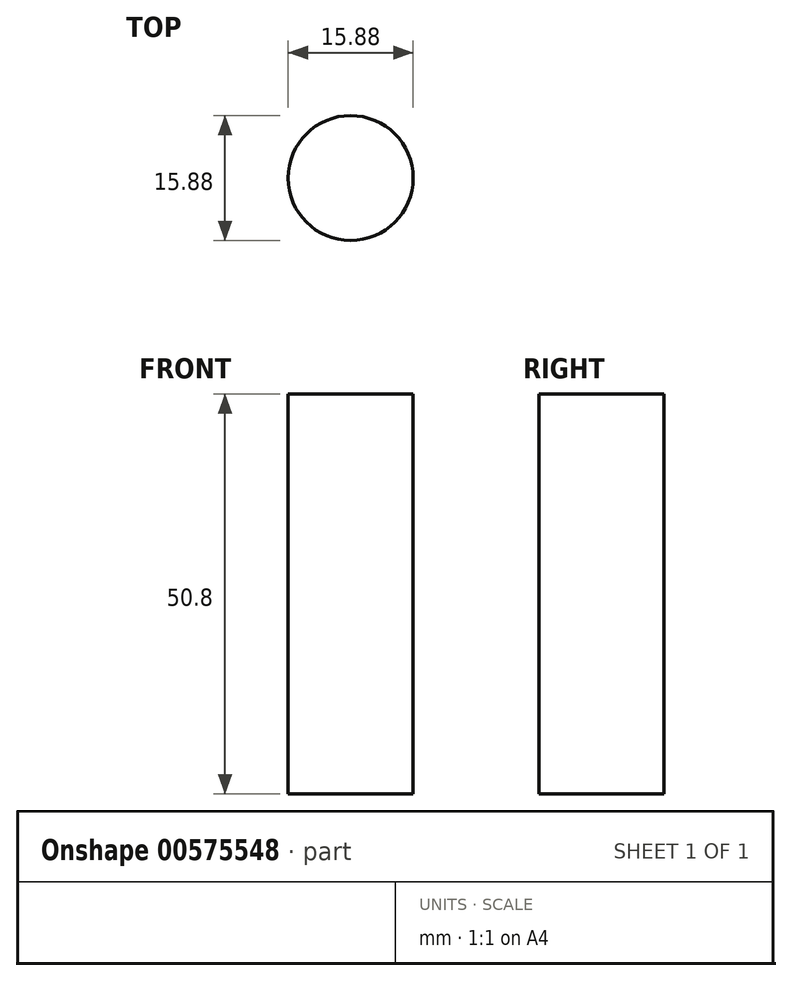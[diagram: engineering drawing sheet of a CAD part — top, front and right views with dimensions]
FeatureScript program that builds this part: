
annotation { "Feature Type Name" : "Feature", "Feature Type Description" : "" }
export const myFeature = defineFeature(function(context is Context, id is Id, definition is map)
    precondition{}
    {
        {
            var Q0;
            Q0=qCreatedBy(makeId("Top.planeOp"),FACE);
            var sketch = newSketch(context, id + "F0", { "sketchPlane" : qUnion([Q0])});
            skCircle(sketch, "E0", {"center": v(0, 0) * mm, "radius": 7.94 * mm});
            skSolve(sketch);
        }
        {
            var Q0;
            Q0=makeQuery(id+"F0.imprint","IMPRINT",FACE,{"disambiguationData":[TD([[makeQuery(id+"F0.imprint","IMPRINT",EDGE,{"derivedFrom":sQuery(id+"F0.wireOp",EDGE,"E0")}),1.0]])]});
            extrude(context, id + "F1", {"entities" : qUnion([Q0]), "endBound" : BoundingType.SYMMETRIC, "depth" : 50.8 * mm, "offsetDistance" : 25.4 * mm});
        }
    });
